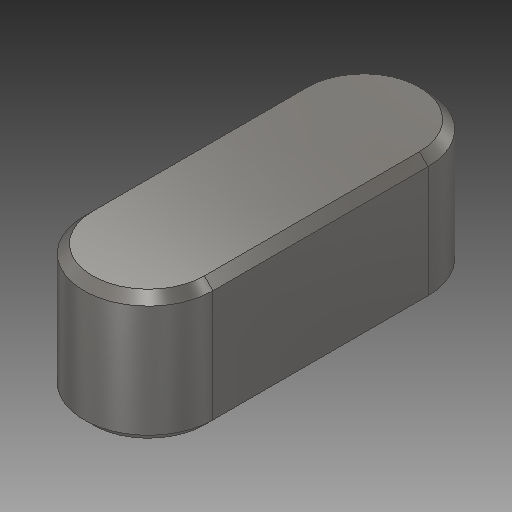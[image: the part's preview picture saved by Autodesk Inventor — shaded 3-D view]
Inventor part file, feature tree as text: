
AUTODESK INVENTOR PART (.ipt)
format: ipt  version: 2019.2 (Build 232265000, 265)  size: 121,344 bytes
history: native  units: mm
features: extrude x1, chamfer x1, sketch x1
ambient origin geometry x8: Origin, YZ Plane, XZ Plane, XY Plane, X Axis, Y Axis, Z Axis, Center Point
bodies: Solid1 (feature_tree)
feature tree (3):
  extrude  "Extrusion1"  Depth=3.0mm
  chamfer  "Chamfer1"  [1 undecoded]
  sketch  "Sketch1"  dims[d1=5.0mm d2=3.0mm d3=0.0mm d4=0.2mm d5=2.0mm d6=45.0deg d7=3.0mm]
note: 1 required parameter value undecoded (feature->parameter linkage not recoverable at this tier; creation-order binding heuristic only, values carry confidence <= 0.55)
